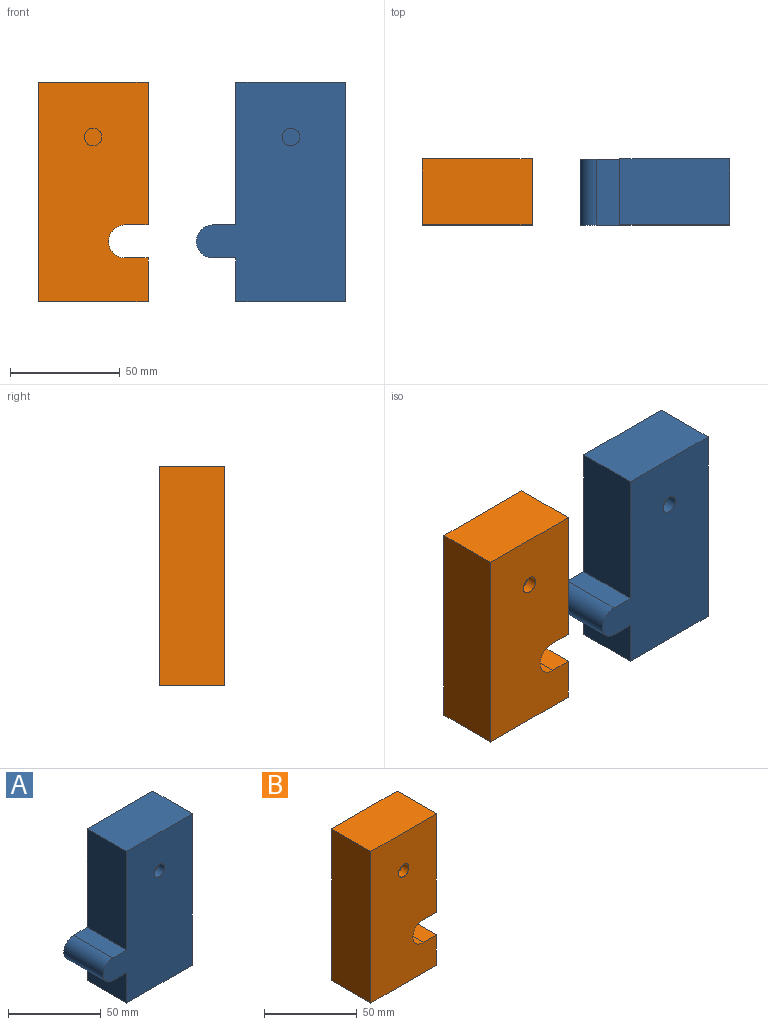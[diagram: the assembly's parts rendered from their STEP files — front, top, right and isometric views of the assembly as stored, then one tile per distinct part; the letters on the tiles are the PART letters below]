
ASSEMBLY  parts=2 mates=1
PART A: 12 faces, bbox 68x30x100 mm
  f0: plane 30x10.5mm, normal (0,0,1), area 315mm2, adj f1,f7,f8,f9
  f1: cylinder r=7.5mm len=30mm, axis (0,1,0), area 706.9mm2, adj f0,f2,f8,f9
  f2: plane 30x10.5mm, normal (0,0,-1), area 315mm2, adj f1,f3,f8,f9
  f3: plane 30x20mm, normal (-1,0,0), area 600mm2, adj f2,f4,f8,f9
  f4: plane 50x30mm, normal (0,0,-1), area 1500mm2, adj f3,f5,f8,f9
  f5: plane 100x30mm, normal (1,0,0), area 3000mm2, adj f4,f6,f8,f9
  f6: plane 50x30mm, normal (0,0,1), area 1500mm2, adj f5,f7,f8,f9
  f7: plane 65x30mm, normal (-1,0,0), area 1950mm2, adj f0,f6,f8,f9
  f8: plane 100x68mm, normal (0,-1,0), area 5195.6mm2, adj f0,f1,f2,f3,f4,f5,f6,f7
  f9: plane 100x68mm, normal (0,1,0), area 5245.9mm2, adj f0,f1,f2,f3,f4,f5,f6,f7
  f10: cylinder r=4mm len=8mm, axis (0,-1,0), area 125.7mm2, adj f8,f11
  f11: plane 8x8mm, normal (0,-1,0), area 50.3mm2, adj f10
PART B: 12 faces, bbox 50x30x100 mm
  f0: plane 30x20mm, normal (1,0,0), area 600mm2, adj f1,f7,f8,f9
  f1: plane 30x10mm, normal (0,0,1), area 300mm2, adj f0,f2,f8,f9
  f2: cylinder r=7.52mm len=30mm, axis (0,1,0), area 737.4mm2, adj f1,f3,f8,f9
  f3: plane 30x10mm, normal (0,0,-1), area 300mm2, adj f2,f4,f8,f9
  f4: plane 65x30mm, normal (1,0,0), area 1950mm2, adj f3,f5,f8,f9
  f5: plane 50x30mm, normal (0,0,1), area 1500mm2, adj f4,f6,f8,f9
  f6: plane 100x30mm, normal (-1,0,0), area 3000mm2, adj f5,f7,f8,f9
  f7: plane 50x30mm, normal (0,0,-1), area 1500mm2, adj f0,f6,f8,f9
  f8: plane 100x50mm, normal (0,-1,0), area 4703.7mm2, adj f0,f1,f2,f3,f4,f5,f6,f7
  f9: plane 100x50mm, normal (0,1,0), area 4754mm2, adj f0,f1,f2,f3,f4,f5,f6,f7
  f10: cylinder r=4mm len=8mm, axis (0,-1,0), area 125.7mm2, adj f8,f11
  f11: plane 8x8mm, normal (0,-1,0), area 50.3mm2, adj f10
PLACE A t=(71.97,-43.22,3.68)mm
PLACE B t=(32.02,-43.22,3.68)mm
MATE slider A.f7 <-> B.f4  axis (-1,0,0) through (71.97,-43.22,21.18)mm
